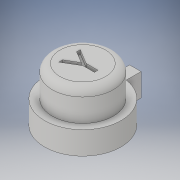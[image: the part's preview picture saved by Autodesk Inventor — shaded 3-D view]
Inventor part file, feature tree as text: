
AUTODESK INVENTOR PART (.ipt)
format: ipt  version: 2019 (Build 230136000, 136)  size: 151,552 bytes
history: native  units: mm
features: extrude x2, sketch x2, revolve x1
ambient origin geometry x8: Origin, YZ Plane, XZ Plane, XY Plane, X Axis, Y Axis, Z Axis, Center Point
bodies: Volumenkörper1 (feature_tree)
feature tree (5):
  revolve  "Umdrehung1"
  extrude  "Extrusion1"  Depth=4.0mm
  extrude  "Extrusion3"  Depth=5.0mm
  sketch  "Skizze2"  dims[d0=2.0mm d1=4.0mm]
  sketch  "Skizze4"  dims[d2=3.0mm d3=5.0mm d4=3.0mm d5=1.0mm d6=1.0mm d7=90.0deg d8=0.5mm d9=0.0mm d15=1.5mm d16=2.0mm d17=0.75mm d18=3.0mm d19=0.0mm]
